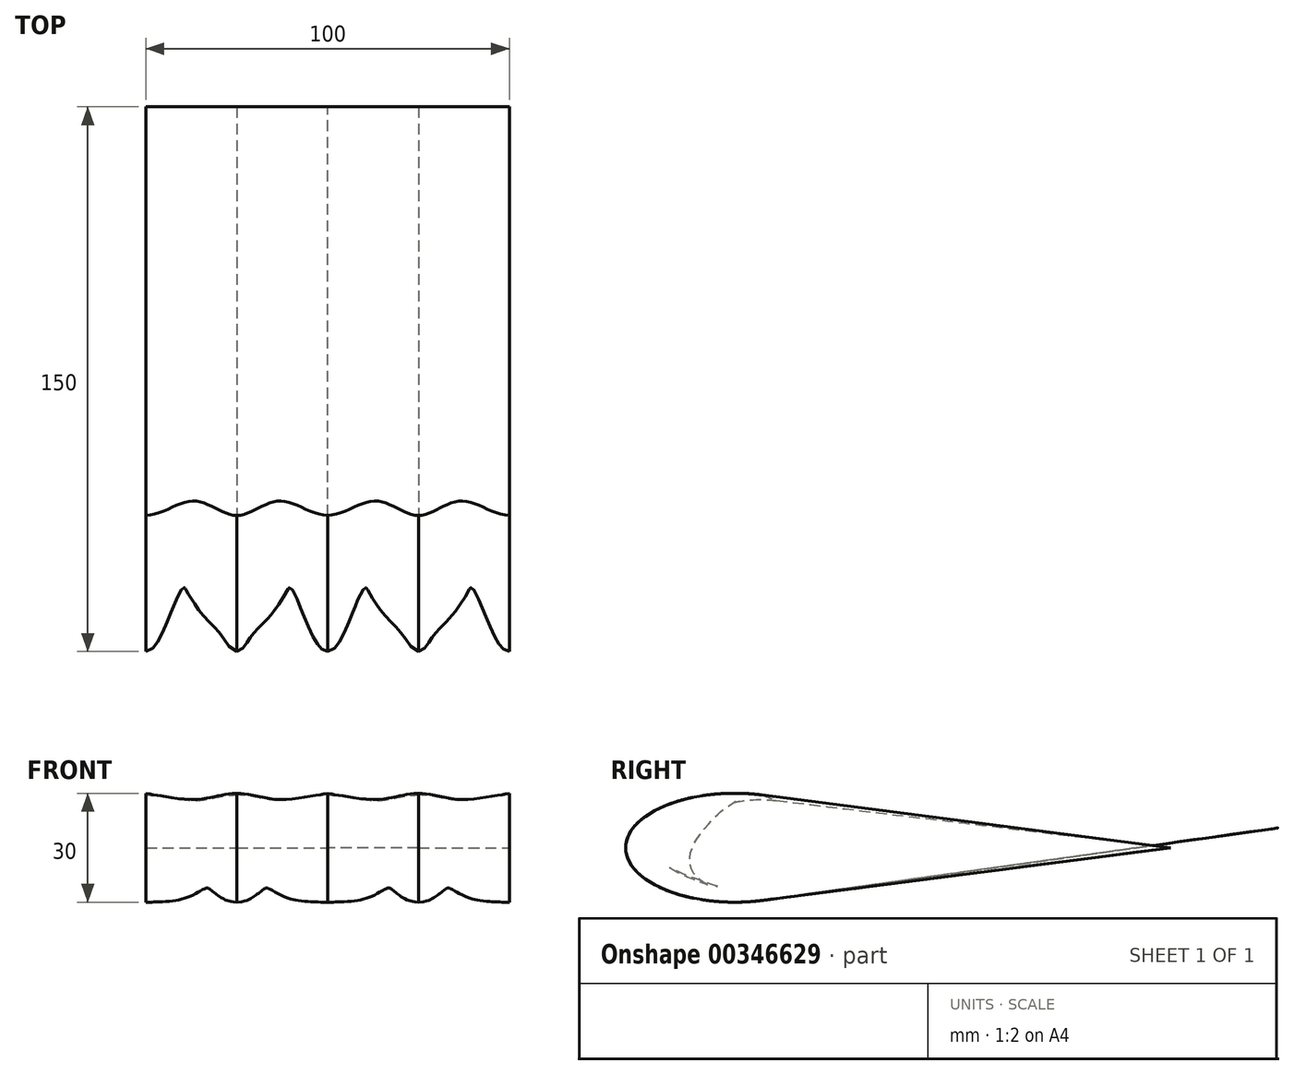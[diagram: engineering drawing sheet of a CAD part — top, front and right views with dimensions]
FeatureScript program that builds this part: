
annotation { "Feature Type Name" : "Feature", "Feature Type Description" : "" }
export const myFeature = defineFeature(function(context is Context, id is Id, definition is map)
    precondition{}
    {
        {
            var Q0;
            Q0=qCreatedBy(makeId("Right.planeOp"),FACE);
            var sketch = newSketch(context, id + "F0", { "sketchPlane" : qUnion([Q0])});
            skEllipse(sketch, "E0", {"center": v(30, 0) * mm, "majorRadius": 30 * mm, "minorRadius": 15 * mm, "majorAxis": v(-1, 0)});
            skLineSegment(sketch, "E1", {"start": v(37.5, 14.52) * mm, "end": v(150, 0) * mm});
            skPoint(sketch, "E1.endSnap0", {"position": v(60, 0) * mm});
            skLineSegment(sketch, "E2", {"start": v(150, 0) * mm, "end": v(37.5, -14.52) * mm});
            skPoint(sketch, "E3", {"position": v(0, 0) * mm});
            skLineSegment(sketch, "E4", {"start": v(30, -15) * mm, "end": v(30, 15) * mm});
            skSolve(sketch);
        }
        {
            var Q0;
            Q0=qCreatedBy(makeId("Right.planeOp"),FACE);
            cPlane(context, id + "F1", {"entities" : qUnion([Q0]), "cplaneType" : CPlaneType.OFFSET, "offset" : 12.5 * mm, "width" : 150 * mm, "height" : 150 * mm});
        }
        {
            var Q0;
            Q0=qCreatedBy(id+"F1.planeOp",FACE);
            var sketch = newSketch(context, id + "F2", { "sketchPlane" : qUnion([Q0])});
            skEllipse(sketch, "E5", {"center": v(37, 0) * mm, "majorRadius": 13.25 * mm, "minorRadius": 22.5 * mm, "majorAxis": v(0, 1)});
            skLineSegment(sketch, "E6", {"start": v(41.48, 12.98) * mm, "end": v(150, 0) * mm});
            skLineSegment(sketch, "E7", {"start": v(150, 0) * mm, "end": v(41.48, -12.98) * mm});
            skPoint(sketch, "E8", {"position": v(14.5, 0) * mm});
            skSolve(sketch);
        }
        {
            var Q0;
            Q0=qCreatedBy(makeId("Right.planeOp"),FACE);
            cPlane(context, id + "F3", {"entities" : qUnion([Q0]), "cplaneType" : CPlaneType.OFFSET, "offset" : 25 * mm, "width" : 150 * mm, "height" : 150 * mm});
        }
        {
            var Q0;
            Q0=qCreatedBy(id+"F3.planeOp",FACE);
            var sketch = newSketch(context, id + "F4", { "sketchPlane" : qUnion([Q0])});
            skEllipse(sketch, "E9", {"center": v(30, 0) * mm, "majorRadius": 30 * mm, "minorRadius": 15 * mm, "majorAxis": v(-1, 0)});
            skLineSegment(sketch, "E10", {"start": v(37.5, 14.52) * mm, "end": v(150, 0) * mm});
            skPoint(sketch, "E10.endSnap0", {"position": v(60, 0) * mm});
            skLineSegment(sketch, "E11", {"start": v(150, 0) * mm, "end": v(37.5, -14.52) * mm});
            skPoint(sketch, "E12", {"position": v(0, 0) * mm});
            skSolve(sketch);
        }
        {
            var Q0;
            {var subQ0=sQuery(id+"F0.wireOp",EDGE,"E1");Q0=makeQuery(id+"F0.imprint","IMPRINT",FACE,{"disambiguationData":[TD([[makeQuery(id+"F0.imprint","IMPRINT",EDGE,{"derivedFrom":subQ0}),-1.0]])]});}
            var Q1;
            {var subQ0=sQuery(id+"F0.wireOp",EDGE,"E0");var subQ1=makeQuery(id+"F0.imprint","INTERSECT",VERTEX,{"derivedFrom":[subQ0,sQuery(id+"F0.wireOp",EDGE,"E1")]});Q1=makeQuery(id+"F0.imprint","IMPRINT",FACE,{"disambiguationData":[TD([[makeQuery(id+"F0.imprint","IMPRINT",EDGE,{"disambiguationData":[TD([[subQ1,1.0]])],"derivedFrom":subQ0}),1.0]])]});}
            var Q2;
            {var subQ0=sQuery(id+"F0.wireOp",EDGE,"E4");Q2=makeQuery(id+"F0.imprint","IMPRINT",FACE,{"disambiguationData":[TD([[makeQuery(id+"F0.imprint","IMPRINT",EDGE,{"derivedFrom":subQ0}),1.0]])]});}
            var Q3;
            {var subQ0=sQuery(id+"F2.wireOp",EDGE,"E5");var subQ1=makeQuery(id+"F2.imprint","INTERSECT",VERTEX,{"derivedFrom":[subQ0,sQuery(id+"F2.wireOp",EDGE,"E6")]});Q3=makeQuery(id+"F2.imprint","IMPRINT",FACE,{"disambiguationData":[TD([[makeQuery(id+"F2.imprint","IMPRINT",EDGE,{"disambiguationData":[TD([[subQ1,1.0]])],"derivedFrom":subQ0}),1.0]])]});}
            var Q4;
            {var subQ0=sQuery(id+"F2.wireOp",EDGE,"E6");Q4=makeQuery(id+"F2.imprint","IMPRINT",FACE,{"disambiguationData":[TD([[makeQuery(id+"F2.imprint","IMPRINT",EDGE,{"derivedFrom":subQ0}),-1.0]])]});}
            var Q5;
            {var subQ0=sQuery(id+"F4.wireOp",EDGE,"E9");var subQ1=makeQuery(id+"F4.imprint","INTERSECT",VERTEX,{"derivedFrom":[subQ0,sQuery(id+"F4.wireOp",EDGE,"E10")]});Q5=makeQuery(id+"F4.imprint","IMPRINT",FACE,{"disambiguationData":[TD([[makeQuery(id+"F4.imprint","IMPRINT",EDGE,{"disambiguationData":[TD([[subQ1,1.0]])],"derivedFrom":subQ0}),1.0]])]});}
            var Q6;
            {var subQ0=sQuery(id+"F4.wireOp",EDGE,"E10");Q6=makeQuery(id+"F4.imprint","IMPRINT",FACE,{"disambiguationData":[TD([[makeQuery(id+"F4.imprint","IMPRINT",EDGE,{"derivedFrom":subQ0}),-1.0]])]});}
            loft(context, id + "F5", {"sheetProfilesArray" : [{ "sheetProfileEntities" : qUnion([Q0, Q1, Q2]) }, { "sheetProfileEntities" : qUnion([Q3, Q4]) }, { "sheetProfileEntities" : qUnion([Q5, Q6]) }], "startCondition" : LoftEndDerivativeType.NORMAL_TO_PROFILE, "startMagnitude" : 1, "endCondition" : LoftEndDerivativeType.NORMAL_TO_PROFILE, "endMagnitude" : 1});
        }
        {
            var Q0;
            {var subQ0=sQuery(id+"F4.wireOp",EDGE,"E9");var subQ1=makeQuery(id+"F4.imprint","INTERSECT",VERTEX,{"derivedFrom":[subQ0,sQuery(id+"F4.wireOp",EDGE,"E10")]});var subQ3=sQuery(id+"F0.wireOp",EDGE,"E0");var subQ4=makeQuery(id+"F0.imprint","INTERSECT",VERTEX,{"derivedFrom":[subQ3,sQuery(id+"F0.wireOp",EDGE,"E1")]});Q0=makeQuery(id+"F5.opLoft","SWEPT_BODY",BODY,{"disambiguationData":[OSD([makeQuery(id+"F0.imprint","IMPRINT",FACE,{"disambiguationData":[TD([[makeQuery(id+"F0.imprint","IMPRINT",EDGE,{"disambiguationData":[TD([[subQ4,1.0]])],"derivedFrom":subQ3}),1.0]])]}),sQuery(id+"F2.wireOp",EDGE,"E5"),makeQuery(id+"F4.imprint","IMPRINT",FACE,{"disambiguationData":[TD([[makeQuery(id+"F4.imprint","IMPRINT",EDGE,{"disambiguationData":[TD([[subQ1,1.0]])],"derivedFrom":subQ0}),1.0]])]})])]});}
            var Q1;
            {var subQ0=sQuery(id+"F4.wireOp",EDGE,"E10");var subQ1=sQuery(id+"F4.wireOp",EDGE,"E9");var subQ2=makeQuery(id+"F4.imprint","INTERSECT",VERTEX,{"derivedFrom":[subQ1,subQ0]});var subQ5=makeQuery(id+"F4.imprint","IMPRINT",EDGE,{"disambiguationData":[TD([[subQ2,1.0]])],"derivedFrom":subQ1});Q1=makeQuery(id+"F5.opLoft","CAP_FACE",FACE,{"disambiguationData":[OSD([makeQuery(id+"F4.imprint","IMPRINT",FACE,{"disambiguationData":[TD([[subQ5,1.0]])]}),makeQuery(id+"F4.imprint","IMPRINT",FACE,{"disambiguationData":[TD([[makeQuery(id+"F4.imprint","IMPRINT",EDGE,{"derivedFrom":subQ0}),-1.0]])]})])],"isStart":true});}
            mirror(context, id + "F6", {"operationType" : NewBodyOperationType.ADD, "entities" : qUnion([Q0]), "mirrorPlane" : qUnion([Q1])});
        }
        {
            var Q0;
            {var subQ0=sQuery(id+"F4.wireOp",EDGE,"E9");var subQ1=makeQuery(id+"F4.imprint","INTERSECT",VERTEX,{"derivedFrom":[subQ0,sQuery(id+"F4.wireOp",EDGE,"E10")]});var subQ3=sQuery(id+"F0.wireOp",EDGE,"E0");var subQ4=makeQuery(id+"F0.imprint","INTERSECT",VERTEX,{"derivedFrom":[subQ3,sQuery(id+"F0.wireOp",EDGE,"E1")]});Q0=makeQuery(id+"F5.opLoft","SWEPT_BODY",BODY,{"disambiguationData":[OSD([makeQuery(id+"F0.imprint","IMPRINT",FACE,{"disambiguationData":[TD([[makeQuery(id+"F0.imprint","IMPRINT",EDGE,{"disambiguationData":[TD([[subQ4,1.0]])],"derivedFrom":subQ3}),1.0]])]}),sQuery(id+"F2.wireOp",EDGE,"E5"),makeQuery(id+"F4.imprint","IMPRINT",FACE,{"disambiguationData":[TD([[makeQuery(id+"F4.imprint","IMPRINT",EDGE,{"disambiguationData":[TD([[subQ1,1.0]])],"derivedFrom":subQ0}),1.0]])]})])]});}
            var Q1;
            {var subQ0=sQuery(id+"F0.wireOp",EDGE,"E1");var subQ1=sQuery(id+"F0.wireOp",EDGE,"E0");var subQ2=makeQuery(id+"F0.imprint","INTERSECT",VERTEX,{"derivedFrom":[subQ1,subQ0]});var subQ5=makeQuery(id+"F0.imprint","IMPRINT",EDGE,{"disambiguationData":[TD([[subQ2,1.0]])],"derivedFrom":subQ1});Q1=makeQuery(id+"F6.opPattern","COPY",FACE,{"derivedFrom":makeQuery(id+"F5.opLoft","CAP_FACE",FACE,{"disambiguationData":[OSD([makeQuery(id+"F0.imprint","IMPRINT",FACE,{"disambiguationData":[TD([[subQ5,1.0]])]}),makeQuery(id+"F0.imprint","IMPRINT",FACE,{"disambiguationData":[TD([[makeQuery(id+"F0.imprint","IMPRINT",EDGE,{"derivedFrom":subQ0}),-1.0]])]})])],"isStart":true}),"instanceName":"1"});}
            mirror(context, id + "F7", {"operationType" : NewBodyOperationType.ADD, "entities" : qUnion([Q0]), "mirrorPlane" : qUnion([Q1])});
        }
    });
